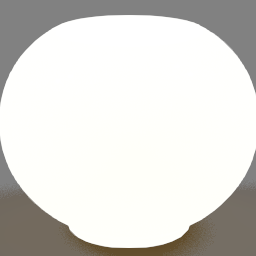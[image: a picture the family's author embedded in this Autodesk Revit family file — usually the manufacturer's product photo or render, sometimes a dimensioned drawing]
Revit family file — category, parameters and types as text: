
# Revit family: 3-030X-xx Skylight Mirror
name_source: partatom
category: Lighting Fixtures
units: mm (PartAtom-declared; Revit-internal decimal feet)

## family parameters
Always vertical = Yes
Cut with Voids When Loaded = No
Host = Wall
Light Source = No
OmniClass Number = 23.80.70.00
OmniClass Title = Lighting
Part Type = Normal
Room Calculation Point = No
Round Connector Dimension = Use Diameter
Shared = No

## types (5) — shared parameters
Diffuser = Ghost Mirror
Lamp = LED Array
Manufacturer = Vanita by Oxygen
Metal Finish 1 = 15 - Black
Model = 3-030X-xx / Skylight
References = Ref. 3 = 120 V / Ref. 37 = 277 V
URL = www.oxygenlighting.com
Voltage = 120 V
Voltage Input = 120 V or 277 V - 50/60 Hz
zero-valued in all types: Default Elevation

## per-type parameters (varying)
| type | Height | Wattage Comments | Width |
| 3-0301-15 / Black | 610 mm  [stored 2.00131 ft] | 1 x 83.5 W at 120 V | 914 mm  [stored 2.99869 ft] |
| 3-0302-15 / Black | 914 mm  [stored 2.99869 ft] | 1 x 99.7 W at 120 V | 914 mm  [stored 2.99869 ft] |
| 3-0303-15 / Black | 914 mm  [stored 2.99869 ft] | 1 x 122.6 W at 120 V | 1219 mm |
| 3-0304-15 / Black | 1219 mm | 1 x 167.9 W at 120 V | 1219 mm |
| 3-0305-15 / Black | 1067 mm  [stored 3.50066 ft] | 1 x 167.9 W at 120 V | 1524 mm  [stored 5 ft] |

note: [stored X ft] marks values corroborated as IEEE doubles in the binary element streams (Revit-internal decimal feet)

## geometry (parser evidence)
native form markers: Sweep x5
no freeform markers — native parametric forms only
